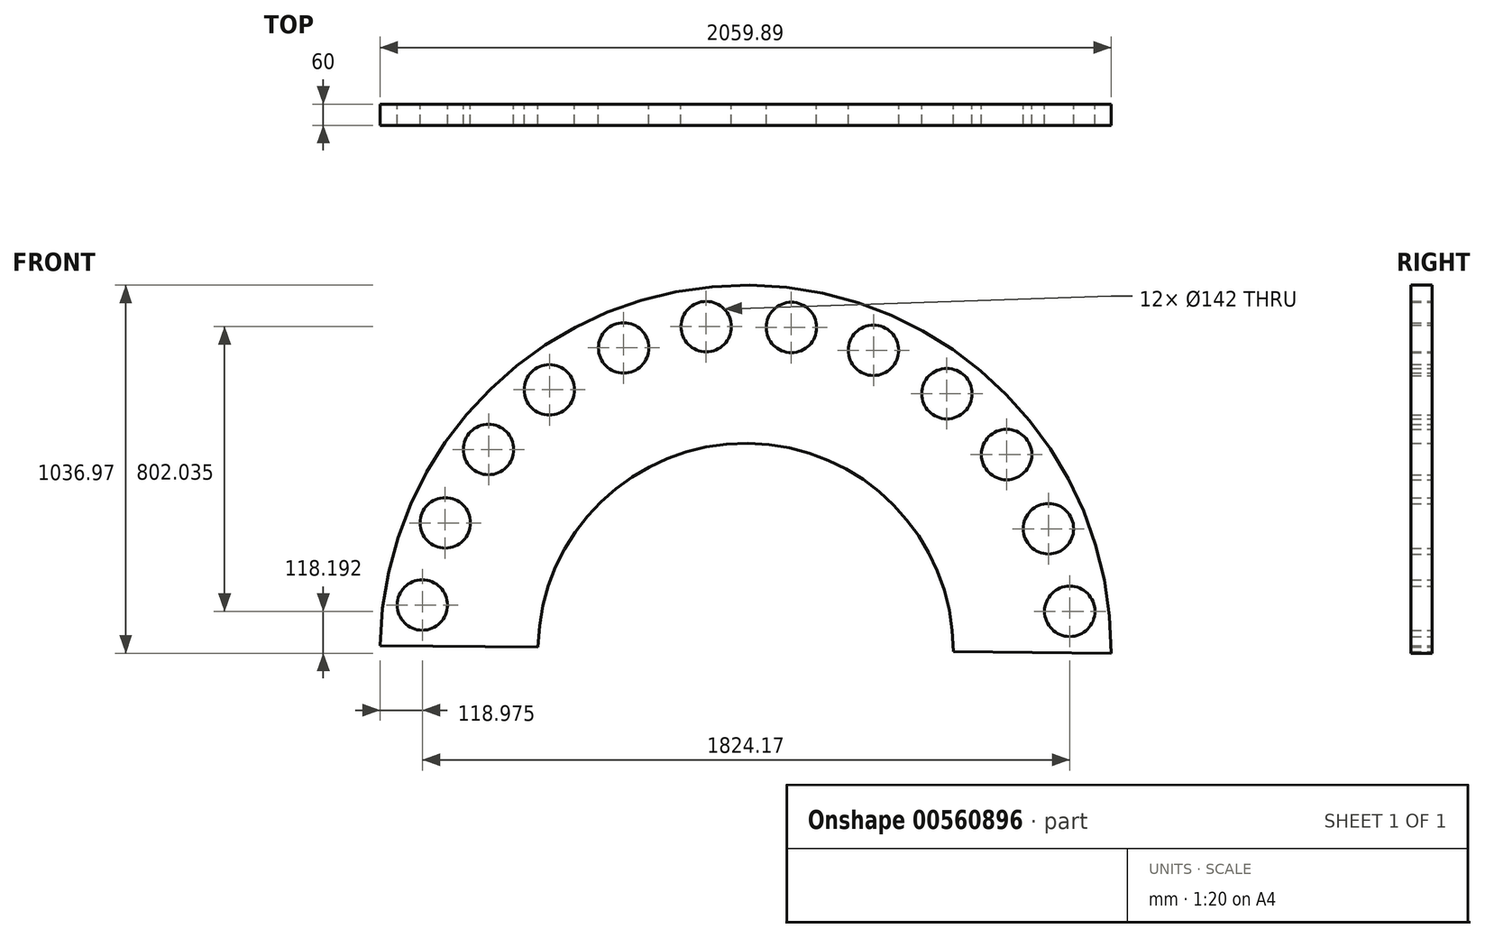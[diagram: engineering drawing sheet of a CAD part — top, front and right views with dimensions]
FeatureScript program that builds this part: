
annotation { "Feature Type Name" : "Feature", "Feature Type Description" : "" }
export const myFeature = defineFeature(function(context is Context, id is Id, definition is map)
    precondition{}
    {
        {
            var Q0;
            Q0=qCreatedBy(makeId("Front.planeOp"),FACE);
            var sketch = newSketch(context, id + "F0", { "sketchPlane" : qUnion([Q0])});
            skArc(sketch, "E0", {"start": v(355.92, 91.07) * mm, "mid": v(-222.84, 678.27) * mm, "end": v(-813.99, 103.54) * mm});
            skLineSegment(sketch, "E1", {"start": v(-813.99, 103.54) * mm, "end": v(355.92, 91.07) * mm, "construction": true});
            skArc(sketch, "E2", {"start": v(-1258.97, 108.28) * mm, "mid": v(-218.1, 1123.24) * mm, "end": v(800.9, 86.33) * mm});
            skLineSegment(sketch, "E3", {"start": v(-1258.97, 108.28) * mm, "end": v(800.9, 86.33) * mm, "construction": true});
            skLineSegment(sketch, "E4", {"start": v(-1258.97, 108.28) * mm, "end": v(-813.99, 103.54) * mm});
            skLineSegment(sketch, "E5", {"start": v(355.92, 91.07) * mm, "end": v(800.9, 86.33) * mm});
            skCircle(sketch, "E6", {"center": v(-229.08, 93.3) * mm, "radius": 920 * mm, "construction": true});
            skCircle(sketch, "E7", {"center": v(-1140, 222.24) * mm, "radius": 71 * mm});
            skLineSegment(sketch, "E8", {"start": v(-229.08, 93.3) * mm, "end": v(-1140, 222.24) * mm, "construction": true});
            skLineSegment(sketch, "E9", {"start": v(-229.08, 93.3) * mm, "end": v(-1526.43, 105.9) * mm, "construction": true});
            skPoint(sketch, "E9.endSnap0", {"position": v(-1036.48, 105.9) * mm});
            skCircle(sketch, "E10.1.0", {"center": v(-1075.58, 453.61) * mm, "radius": 71 * mm});
            skCircle(sketch, "E10.2.0", {"center": v(-953.49, 660.43) * mm, "radius": 71 * mm});
            skCircle(sketch, "E10.3.0", {"center": v(-782.02, 828.6) * mm, "radius": 71 * mm});
            skCircle(sketch, "E10.4.0", {"center": v(-572.87, 946.65) * mm, "radius": 71 * mm});
            skCircle(sketch, "E10.5.0", {"center": v(-340.3, 1006.56) * mm, "radius": 71 * mm});
            skCircle(sketch, "E10.6.0", {"center": v(-100.14, 1004.22) * mm, "radius": 71 * mm});
            skCircle(sketch, "E10.7.0", {"center": v(131.23, 939.81) * mm, "radius": 71 * mm});
            skCircle(sketch, "E10.8.0", {"center": v(338.05, 817.71) * mm, "radius": 71 * mm});
            skCircle(sketch, "E10.9.0", {"center": v(506.22, 646.25) * mm, "radius": 71 * mm});
            skCircle(sketch, "E10.10.0", {"center": v(624.27, 437.1) * mm, "radius": 71 * mm});
            skCircle(sketch, "E10.11.0", {"center": v(684.18, 204.52) * mm, "radius": 71 * mm});
            skLineSegment(sketch, "E10.anchor2", {"start": v(-229.08, 93.3) * mm, "end": v(684.18, 204.52) * mm, "construction": true});
            skSolve(sketch);
        }
        {
            var Q0;
            Q0 = qSketchRegion(id + "F0", true);
            extrude(context, id + "F1", {"entities" : qUnion([Q0]), "depth" : 60 * mm, "offsetDistance" : 25 * mm});
        }
    });
